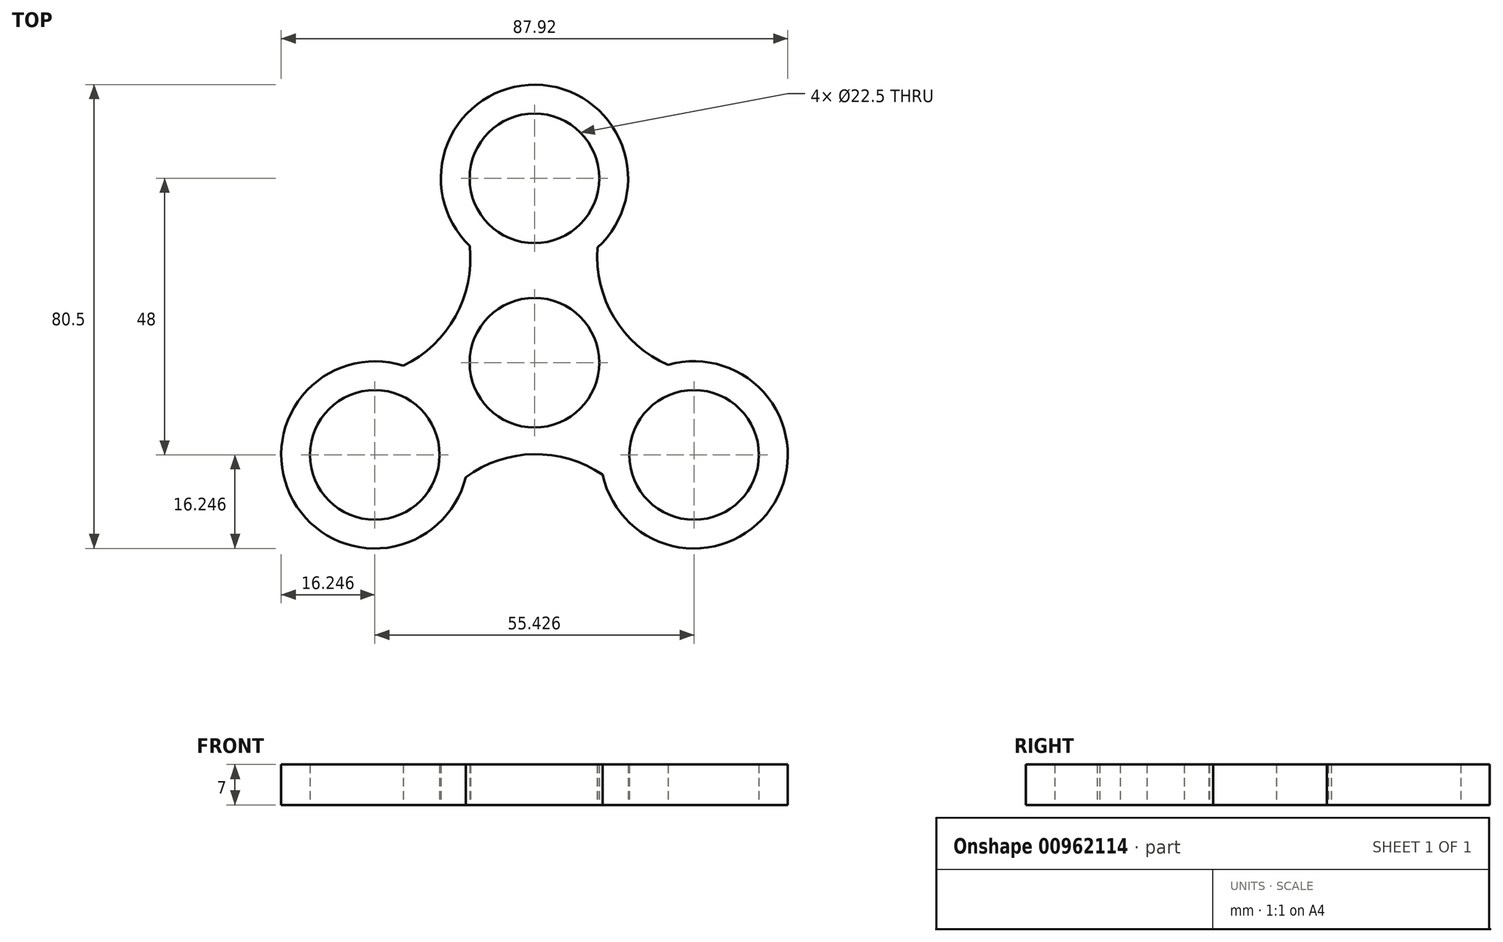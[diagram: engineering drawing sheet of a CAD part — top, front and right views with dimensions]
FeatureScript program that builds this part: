
annotation { "Feature Type Name" : "Feature", "Feature Type Description" : "" }
export const myFeature = defineFeature(function(context is Context, id is Id, definition is map)
    precondition{}
    {
        {
            var Q0;
            Q0=qCreatedBy(makeId("Top.planeOp"),FACE);
            var sketch = newSketch(context, id + "F0", { "sketchPlane" : qUnion([Q0])});
            skCircle(sketch, "E0", {"center": v(-927.31, 374.8) * mm, "radius": 11.25 * mm});
            skCircle(sketch, "E1", {"center": v(-927.31, 406.8) * mm, "radius": 11.25 * mm});
            skPoint(sketch, "E2.center", {"position": v(-930.17, 379.8) * mm});
            skCircle(sketch, "E3.1.0", {"center": v(-955.02, 358.8) * mm, "radius": 11.25 * mm});
            skCircle(sketch, "E3.2.0", {"center": v(-899.6, 358.8) * mm, "radius": 11.25 * mm});
            skCircle(sketch, "E4.0", {"center": v(-955.02, 358.8) * mm, "radius": 16.25 * mm});
            skCircle(sketch, "E5.0", {"center": v(-899.6, 358.8) * mm, "radius": 16.25 * mm});
            skCircle(sketch, "E6.0", {"center": v(-927.31, 406.8) * mm, "radius": 16.25 * mm});
            skArc(sketch, "E7", {"start": v(-950.08, 374.29) * mm, "mid": v(-941, 382.85) * mm, "end": v(-938.56, 395.07) * mm});
            skArc(sketch, "E8.1.0", {"start": v(-915.48, 355.34) * mm, "mid": v(-927.42, 358.92) * mm, "end": v(-939.24, 354.93) * mm});
            skArc(sketch, "E8.2.0", {"start": v(-916.37, 394.79) * mm, "mid": v(-913.5, 382.65) * mm, "end": v(-904.14, 374.4) * mm});
            skSolve(sketch);
        }
        {
            var Q0;
            Q0=makeQuery(id+"F0.imprint","IMPRINT",FACE,{"disambiguationData":[TD([[makeQuery(id+"F0.imprint","IMPRINT",EDGE,{"derivedFrom":sQuery(id+"F0.wireOp",EDGE,"E1")}),-1.0]])]});
            var Q1;
            Q1=makeQuery(id+"F0.imprint","IMPRINT",FACE,{"disambiguationData":[TD([[makeQuery(id+"F0.imprint","IMPRINT",EDGE,{"derivedFrom":sQuery(id+"F0.wireOp",EDGE,"E0")}),-1.0]])]});
            var Q2;
            Q2=makeQuery(id+"F0.imprint","IMPRINT",FACE,{"disambiguationData":[TD([[makeQuery(id+"F0.imprint","IMPRINT",EDGE,{"derivedFrom":sQuery(id+"F0.wireOp",EDGE,"E3.2.0")}),-1.0]])]});
            var Q3;
            Q3=makeQuery(id+"F0.imprint","IMPRINT",FACE,{"disambiguationData":[TD([[makeQuery(id+"F0.imprint","IMPRINT",EDGE,{"derivedFrom":sQuery(id+"F0.wireOp",EDGE,"E3.1.0")}),-1.0]])]});
            extrude(context, id + "F1", {"entities" : qUnion([Q0, Q1, Q2, Q3]), "depth" : 7 * mm, "offsetDistance" : 25 * mm});
        }
    });
